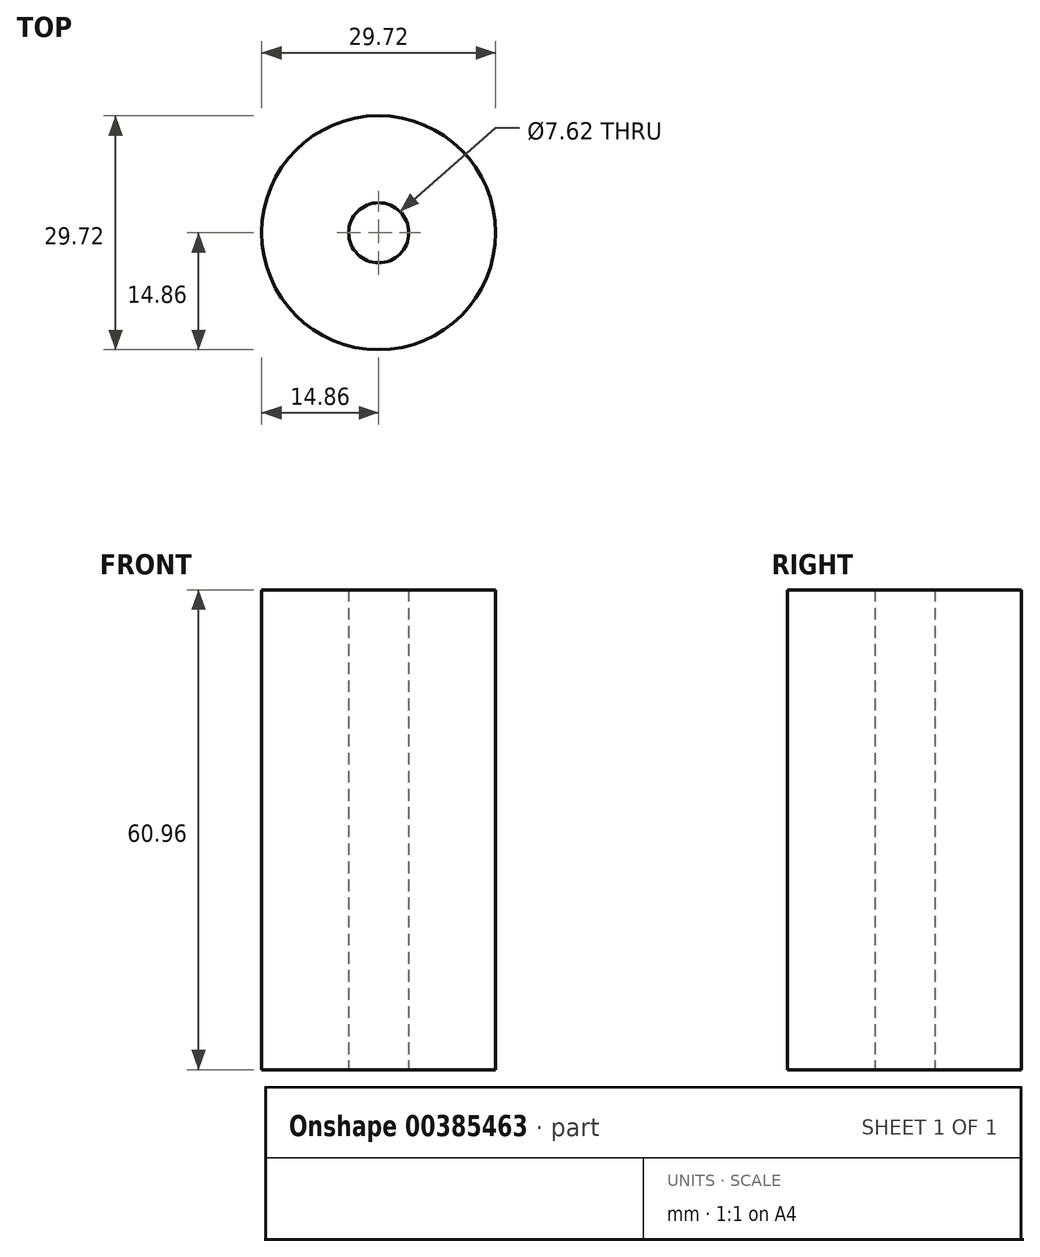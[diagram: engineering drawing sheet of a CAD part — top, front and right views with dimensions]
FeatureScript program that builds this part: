
annotation { "Feature Type Name" : "Feature", "Feature Type Description" : "" }
export const myFeature = defineFeature(function(context is Context, id is Id, definition is map)
    precondition{}
    {
        {
            var Q0;
            Q0=qCreatedBy(makeId("Top.planeOp"),FACE);
            var sketch = newSketch(context, id + "F0", { "sketchPlane" : qUnion([Q0])});
            skCircle(sketch, "E0", {"center": v(0, 0) * mm, "radius": 3.81 * mm});
            skCircle(sketch, "E1", {"center": v(0, 0) * mm, "radius": 14.86 * mm});
            skSolve(sketch);
        }
        {
            var Q0;
            Q0 = qSketchRegion(id + "F0", true);
            extrude(context, id + "F1", {"entities" : qUnion([Q0]), "depth" : 60.96 * mm});
        }
    });
